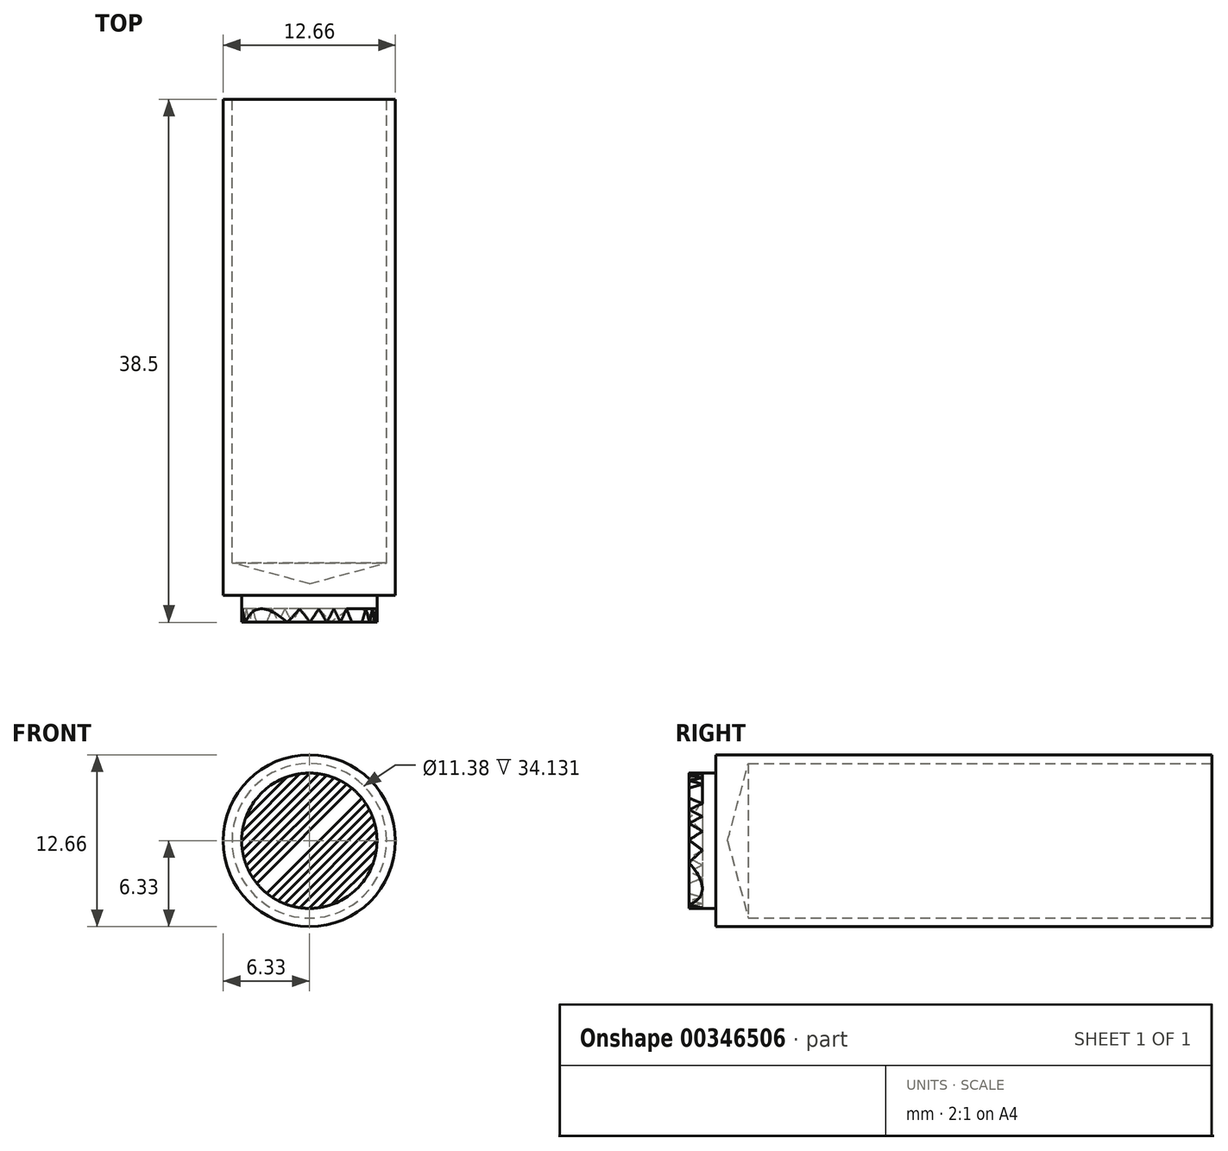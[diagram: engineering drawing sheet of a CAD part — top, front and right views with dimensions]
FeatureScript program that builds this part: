
annotation { "Feature Type Name" : "Feature", "Feature Type Description" : "" }
export const myFeature = defineFeature(function(context is Context, id is Id, definition is map)
    precondition{}
    {
        {
            var Q0;
            Q0=qCreatedBy(makeId("Right.planeOp"),FACE);
            var sketch = newSketch(context, id + "F0", { "sketchPlane" : qUnion([Q0])});
            skLineSegment(sketch, "E0", {"start": v(0, 0) * mm, "end": v(-38.5, 0) * mm});
            skLineSegment(sketch, "E1", {"start": v(-38.5, 0) * mm, "end": v(-38.5, 4.98) * mm});
            skLineSegment(sketch, "E2", {"start": v(-38.5, 4.98) * mm, "end": v(-36.51, 4.98) * mm});
            skLineSegment(sketch, "E3", {"start": v(-36.51, 4.98) * mm, "end": v(-36.51, 6.33) * mm});
            skLineSegment(sketch, "E4", {"start": v(-36.51, 6.33) * mm, "end": v(0, 6.33) * mm});
            skLineSegment(sketch, "E5", {"start": v(0, 0) * mm, "end": v(0, 6.33) * mm});
            skLineSegment(sketch, "E6", {"start": v(0, 0) * mm, "end": v(15.88, 0) * mm, "construction": true});
            skSolve(sketch);
        }
        {
            var Q0;
            Q0 = qSketchRegion(id + "F0", true);
            var Q1;
            Q1=sQuery(id+"F0.wireOp",EDGE,"E6");
            revolve(context, id + "F1", {"entities" : qUnion([Q0]), "axis" : qUnion([Q1]), "revolveType" : RevolveType.FULL});
        }
        {
            var Q0;
            Q0=qCreatedBy(makeId("Right.planeOp"),FACE);
            var sketch = newSketch(context, id + "F2", { "sketchPlane" : qUnion([Q0])});
            skLineSegment(sketch, "E7", {"start": v(0, 0) * mm, "end": v(10.43, 0) * mm, "construction": true});
            skLineSegment(sketch, "E8", {"start": v(-34.13, 5.69) * mm, "end": v(0, 5.69) * mm});
            skLineSegment(sketch, "E9.0", {"start": v(0, 0) * mm, "end": v(0, 5.69) * mm});
            skPoint(sketch, "E10.orphan", {"position": v(0, -6.33) * mm});
            skLineSegment(sketch, "E11", {"start": v(0, 0) * mm, "end": v(-35.66, 0) * mm});
            skLineSegment(sketch, "E12", {"start": v(-34.13, 5.69) * mm, "end": v(-35.66, 0) * mm});
            skPoint(sketch, "E13.orphan", {"position": v(-35.74, 0) * mm});
            skPoint(sketch, "E14.orphan", {"position": v(0, 6.33) * mm});
            skSolve(sketch);
        }
        {
            var Q0;
            Q0 = qSketchRegion(id + "F2", true);
            var Q1;
            Q1=sQuery(id+"F2.wireOp",EDGE,"E7");
            revolve(context, id + "F3", {"operationType" : NewBodyOperationType.REMOVE, "entities" : qUnion([Q0]), "axis" : qUnion([Q1]), "revolveType" : RevolveType.FULL, "oppositeDirection" : true});
        }
        {
            var Q0;
            Q0=qCreatedBy(makeId("Right.planeOp"),FACE);
            var sketch = newSketch(context, id + "F4", { "sketchPlane" : qUnion([Q0])});
            skLineSegment(sketch, "E15", {"start": v(0, 0) * mm, "end": v(-58.96, 0) * mm, "construction": true});
            skSolve(sketch);
        }
        {
            var Q0;
            Q0=sQuery(id+"F4.wireOp",EDGE,"E15");
            var Q1;
            Q1=qCreatedBy(makeId("Right.planeOp"),FACE);
            cPlane(context, id + "F5", {"entities" : qUnion([Q0, Q1]), "cplaneType" : CPlaneType.LINE_ANGLE, "offset" : 25.4 * mm, "angle" : 45 * degree, "width" : 152.4 * mm, "height" : 152.4 * mm});
        }
        {
            var Q0;
            Q0=qCreatedBy(id+"F5.planeOp",FACE);
            var sketch = newSketch(context, id + "F6", { "sketchPlane" : qUnion([Q0])});
            skLineSegment(sketch, "E16.0", {"start": v(38.5, 4.98) * mm, "end": v(38.5, -4.98) * mm, "construction": true});
            skLineSegment(sketch, "E17", {"start": v(38.5, 4.48) * mm, "end": v(37.5, 4.48) * mm, "construction": true});
            skLineSegment(sketch, "E18", {"start": v(37.5, 4.48) * mm, "end": v(37.5, 0) * mm, "construction": true});
            skLineSegment(sketch, "E19", {"start": v(38.5, 4.48) * mm, "end": v(37.5, 3.99) * mm});
            skLineSegment(sketch, "E20", {"start": v(38.5, 4.48) * mm, "end": v(37.5, 4.98) * mm});
            skLineSegment(sketch, "E21", {"start": v(37.5, 4.48) * mm, "end": v(37.5, 4.98) * mm, "construction": true});
            skLineSegment(sketch, "E22", {"start": v(38.5, 4.98) * mm, "end": v(36.31, 4.98) * mm, "construction": true});
            skLineSegment(sketch, "E23.0.1.0", {"start": v(38.5, 3.5) * mm, "end": v(37.5, 3) * mm});
            skLineSegment(sketch, "E23.0.1.1", {"start": v(38.5, 3.5) * mm, "end": v(37.5, 3.99) * mm});
            skLineSegment(sketch, "E23.0.1.2", {"start": v(38.5, 3.5) * mm, "end": v(37.5, 3.5) * mm, "construction": true});
            skLineSegment(sketch, "E23.0.2.0", {"start": v(38.5, 2.5) * mm, "end": v(37.5, 2) * mm});
            skLineSegment(sketch, "E23.0.2.1", {"start": v(38.5, 2.5) * mm, "end": v(37.5, 3) * mm});
            skLineSegment(sketch, "E23.0.2.2", {"start": v(38.5, 2.5) * mm, "end": v(37.5, 2.5) * mm, "construction": true});
            skLineSegment(sketch, "E23.0.3.0", {"start": v(38.5, 1.51) * mm, "end": v(37.5, 1.02) * mm});
            skLineSegment(sketch, "E23.0.3.1", {"start": v(38.5, 1.51) * mm, "end": v(37.5, 2) * mm});
            skLineSegment(sketch, "E23.0.3.2", {"start": v(38.5, 1.51) * mm, "end": v(37.5, 1.51) * mm, "construction": true});
            skLineSegment(sketch, "E23.1.0.0", {"start": v(63.9, 4.48) * mm, "end": v(62.9, 3.99) * mm});
            skLineSegment(sketch, "E23.1.0.1", {"start": v(63.9, 4.48) * mm, "end": v(62.9, 4.98) * mm});
            skLineSegment(sketch, "E23.1.0.2", {"start": v(63.9, 4.48) * mm, "end": v(62.9, 4.48) * mm, "construction": true});
            skLineSegment(sketch, "E23.1.1.0", {"start": v(63.9, 3.5) * mm, "end": v(62.9, 3) * mm});
            skLineSegment(sketch, "E23.1.1.1", {"start": v(63.9, 3.5) * mm, "end": v(62.9, 3.99) * mm});
            skLineSegment(sketch, "E23.1.1.2", {"start": v(63.9, 3.5) * mm, "end": v(62.9, 3.5) * mm, "construction": true});
            skLineSegment(sketch, "E23.1.2.0", {"start": v(63.9, 2.5) * mm, "end": v(62.9, 2) * mm});
            skLineSegment(sketch, "E23.1.2.1", {"start": v(63.9, 2.5) * mm, "end": v(62.9, 3) * mm});
            skLineSegment(sketch, "E23.1.2.2", {"start": v(63.9, 2.5) * mm, "end": v(62.9, 2.5) * mm, "construction": true});
            skLineSegment(sketch, "E23.1.3.0", {"start": v(63.9, 1.51) * mm, "end": v(62.9, 1.02) * mm});
            skLineSegment(sketch, "E23.1.3.1", {"start": v(63.9, 1.51) * mm, "end": v(62.9, 2) * mm});
            skLineSegment(sketch, "E23.1.3.2", {"start": v(63.9, 1.51) * mm, "end": v(62.9, 1.51) * mm, "construction": true});
            skLineSegment(sketch, "E23.2.0.0", {"start": v(89.3, 4.48) * mm, "end": v(88.3, 3.99) * mm});
            skLineSegment(sketch, "E23.2.0.1", {"start": v(89.3, 4.48) * mm, "end": v(88.3, 4.98) * mm});
            skLineSegment(sketch, "E23.2.0.2", {"start": v(89.3, 4.48) * mm, "end": v(88.3, 4.48) * mm, "construction": true});
            skLineSegment(sketch, "E23.2.1.0", {"start": v(89.3, 3.5) * mm, "end": v(88.3, 3) * mm});
            skLineSegment(sketch, "E23.2.1.1", {"start": v(89.3, 3.5) * mm, "end": v(88.3, 3.99) * mm});
            skLineSegment(sketch, "E23.2.1.2", {"start": v(89.3, 3.5) * mm, "end": v(88.3, 3.5) * mm, "construction": true});
            skLineSegment(sketch, "E23.2.2.0", {"start": v(89.3, 2.5) * mm, "end": v(88.3, 2) * mm});
            skLineSegment(sketch, "E23.2.2.1", {"start": v(89.3, 2.5) * mm, "end": v(88.3, 3) * mm});
            skLineSegment(sketch, "E23.2.2.2", {"start": v(89.3, 2.5) * mm, "end": v(88.3, 2.5) * mm, "construction": true});
            skLineSegment(sketch, "E23.2.3.0", {"start": v(89.3, 1.51) * mm, "end": v(88.3, 1.02) * mm});
            skLineSegment(sketch, "E23.2.3.1", {"start": v(89.3, 1.51) * mm, "end": v(88.3, 2) * mm});
            skLineSegment(sketch, "E23.2.3.2", {"start": v(89.3, 1.51) * mm, "end": v(88.3, 1.51) * mm, "construction": true});
            skLineSegment(sketch, "E23.direction1", {"start": v(37.5, 3.99) * mm, "end": v(62.9, 3.99) * mm, "construction": true});
            skLineSegment(sketch, "E23.direction2", {"start": v(37.5, 3.99) * mm, "end": v(37.5, 3) * mm, "construction": true});
            skLineSegment(sketch, "E24.MirrorCS", {"start": v(38.5, -2.5) * mm, "end": v(37.5, -2.5) * mm, "construction": true});
            skLineSegment(sketch, "E25.MirrorCS", {"start": v(38.5, -2.5) * mm, "end": v(37.5, -3) * mm});
            skLineSegment(sketch, "E26.MirrorCS", {"start": v(38.5, -2.5) * mm, "end": v(37.5, -2) * mm});
            skLineSegment(sketch, "E27.MirrorCS", {"start": v(38.5, -3.5) * mm, "end": v(37.5, -3.5) * mm, "construction": true});
            skLineSegment(sketch, "E28.MirrorCS", {"start": v(38.5, -3.5) * mm, "end": v(37.5, -3.99) * mm});
            skLineSegment(sketch, "E29.MirrorCS", {"start": v(38.5, -3.5) * mm, "end": v(37.5, -3) * mm});
            skLineSegment(sketch, "E30.MirrorCS", {"start": v(37.5, -4.48) * mm, "end": v(37.5, -4.98) * mm, "construction": true});
            skLineSegment(sketch, "E31.MirrorCS", {"start": v(38.5, -4.48) * mm, "end": v(37.5, -4.98) * mm});
            skLineSegment(sketch, "E32.MirrorCS", {"start": v(38.5, -4.48) * mm, "end": v(37.5, -3.99) * mm});
            skLineSegment(sketch, "E33.MirrorCS", {"start": v(38.5, -4.48) * mm, "end": v(37.5, -4.48) * mm, "construction": true});
            skLineSegment(sketch, "E34.MirrorCS", {"start": v(37.5, -3.99) * mm, "end": v(37.5, -3) * mm, "construction": true});
            skLineSegment(sketch, "E35.MirrorCS", {"start": v(38.5, -1.51) * mm, "end": v(37.5, -1.51) * mm, "construction": true});
            skLineSegment(sketch, "E36.MirrorCS", {"start": v(38.5, -1.51) * mm, "end": v(37.5, -2) * mm});
            skLineSegment(sketch, "E37.MirrorCS", {"start": v(38.5, -1.51) * mm, "end": v(37.5, -1.02) * mm});
            skLineSegment(sketch, "E38", {"start": v(37.5, -1.02) * mm, "end": v(38.5, -0.52) * mm});
            skLineSegment(sketch, "E39", {"start": v(37.5, 1.02) * mm, "end": v(38.5, 0.52) * mm});
            skLineSegment(sketch, "E40", {"start": v(38.5, 0.52) * mm, "end": v(38.5, -0.52) * mm});
            skLineSegment(sketch, "E41", {"start": v(37.5, -4.98) * mm, "end": v(37.5, -6.67) * mm});
            skLineSegment(sketch, "E42", {"start": v(37.5, -6.67) * mm, "end": v(39.6, -6.67) * mm});
            skLineSegment(sketch, "E43", {"start": v(39.6, -6.67) * mm, "end": v(39.6, 6.71) * mm});
            skLineSegment(sketch, "E44", {"start": v(39.6, 6.71) * mm, "end": v(37.5, 6.71) * mm});
            skLineSegment(sketch, "E45", {"start": v(37.5, 4.98) * mm, "end": v(37.5, 6.71) * mm});
            skSolve(sketch);
        }
        {
            var Q0;
            Q0 = qSketchRegion(id + "F6", true);
            extrude(context, id + "F7", {"entities" : qUnion([Q0]), "operationType" : NewBodyOperationType.REMOVE, "endBound" : BoundingType.THROUGH_ALL, "oppositeDirection" : true, "depth" : 25.4 * mm, "hasSecondDirection" : true, "secondDirectionOppositeDirection" : false, "secondDirectionDepth" : 25.4 * mm});
        }
    });
